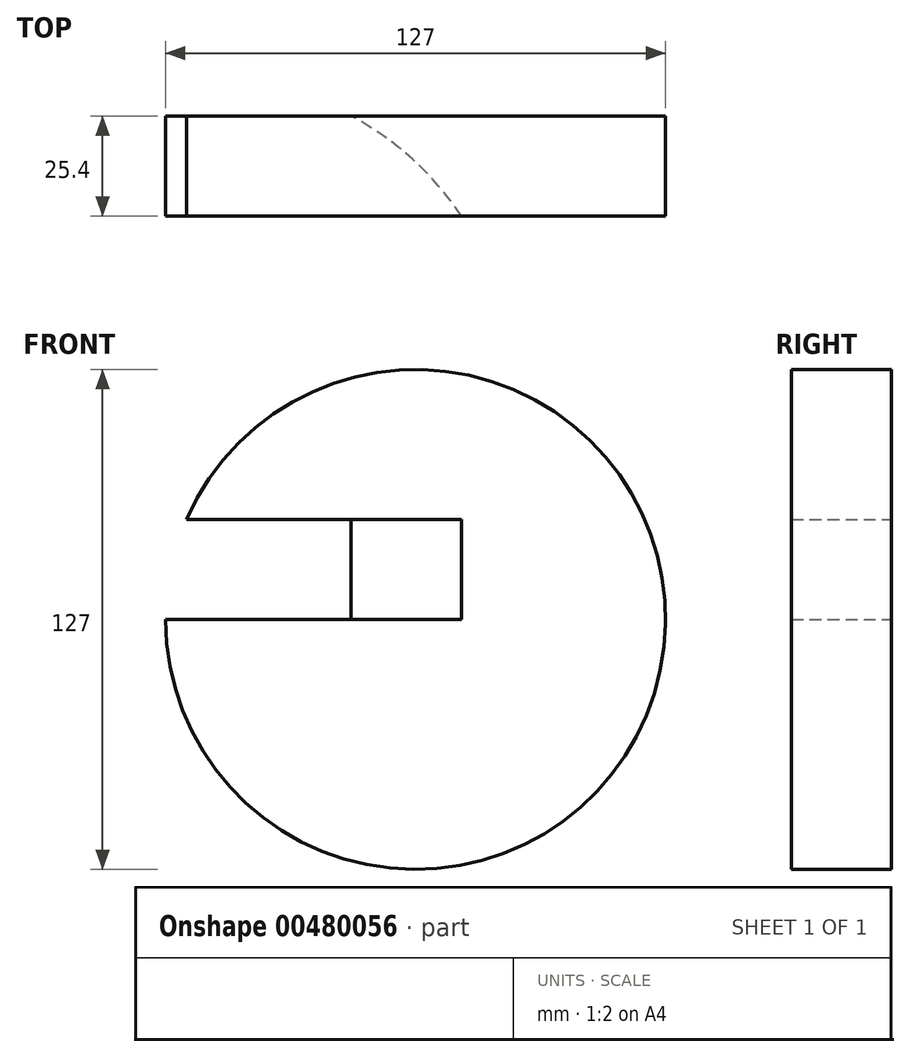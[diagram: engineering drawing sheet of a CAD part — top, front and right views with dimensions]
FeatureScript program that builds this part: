
annotation { "Feature Type Name" : "Feature", "Feature Type Description" : "" }
export const myFeature = defineFeature(function(context is Context, id is Id, definition is map)
    precondition{}
    {
        {
            var Q0;
            Q0=qCreatedBy(makeId("Front.planeOp"),FACE);
            var sketch = newSketch(context, id + "F0", { "sketchPlane" : qUnion([Q0])});
            skCircle(sketch, "E0", {"center": v(0, 0) * mm, "radius": 63.5 * mm});
            skSolve(sketch);
        }
        {
            var Q0;
            Q0 = qSketchRegion(id + "F0", true);
            extrude(context, id + "F1", {"entities" : qUnion([Q0]), "depth" : 25.4 * mm});
        }
        {
            var Q0;
            Q0=qCreatedBy(makeId("Top.planeOp"),FACE);
            var sketch = newSketch(context, id + "F2", { "sketchPlane" : qUnion([Q0])});
            skCircle(sketch, "E1", {"center": v(-51.97, -67.37) * mm, "radius": 76.2 * mm});
            skSolve(sketch);
        }
        {
            var Q0;
            Q0=makeQuery(id+"F2.imprint","IMPRINT",FACE,{"disambiguationData":[TD([[makeQuery(id+"F2.imprint","IMPRINT",EDGE,{"derivedFrom":sQuery(id+"F2.wireOp",EDGE,"E1")}),1.0]])]});
            extrude(context, id + "F3", {"entities" : qUnion([Q0]), "depth" : 25.4 * mm});
        }
        {
            var Q0;
            Q0=makeQuery(id+"F3.opExtrude","SWEPT_BODY",BODY,{"disambiguationData":[OSD([sQuery(id+"F2.wireOp",EDGE,"E1")])]});
            var Q1;
            Q1=makeQuery(id+"F1.opExtrude","SWEPT_BODY",BODY,{"disambiguationData":[OSD([sQuery(id+"F0.wireOp",EDGE,"E0")])]});
            booleanBodies(context, id + "F4", {"operationType" : BooleanOperationType.SUBTRACTION, "tools" : qUnion([Q0]), "targets" : qUnion([Q1])});
        }
    });
